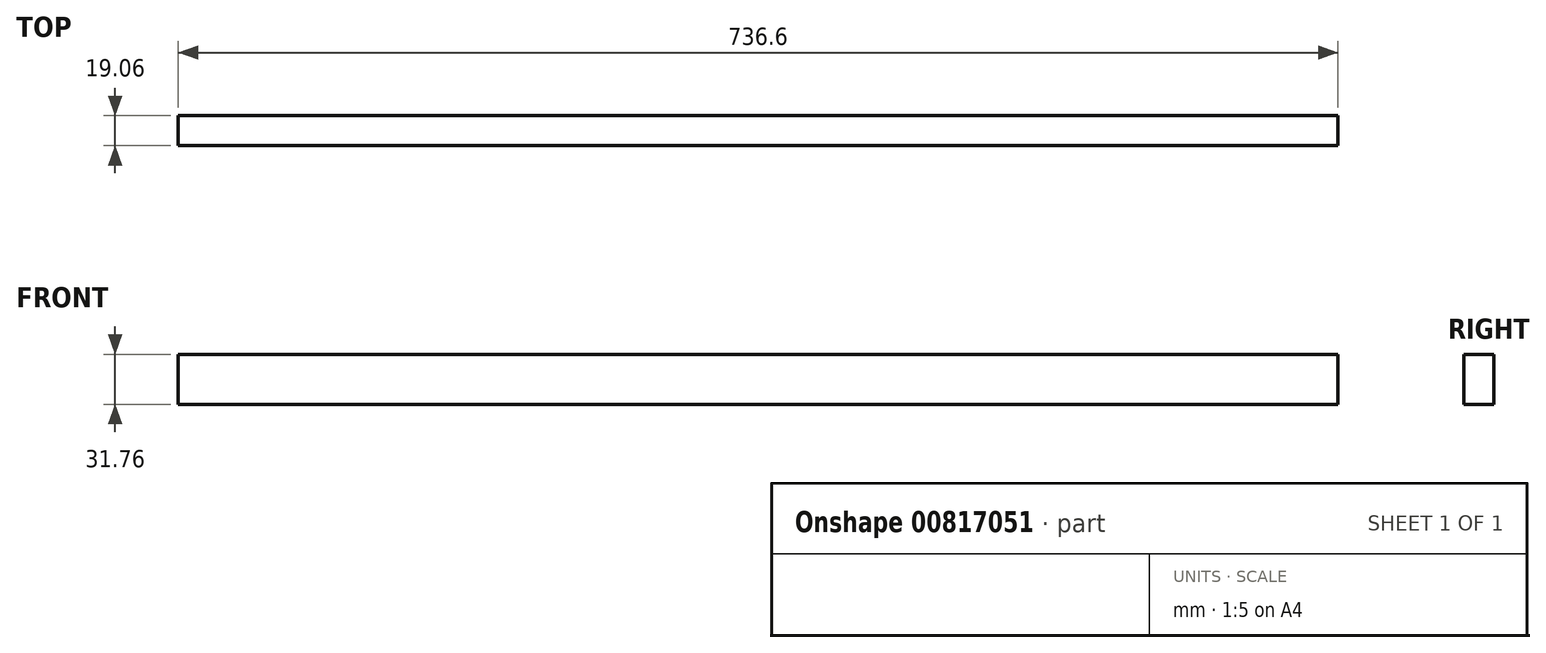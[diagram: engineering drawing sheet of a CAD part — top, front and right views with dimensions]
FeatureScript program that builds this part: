
annotation { "Feature Type Name" : "Feature", "Feature Type Description" : "" }
export const myFeature = defineFeature(function(context is Context, id is Id, definition is map)
    precondition{}
    {
        {
            var Q0;
            Q0=qCreatedBy(makeId("Right.planeOp"),FACE);
            var sketch = newSketch(context, id + "F0", { "sketchPlane" : qUnion([Q0])});
            skLineSegment(sketch, "E0.bottom", {"start": v(9.52, 15.88) * mm, "end": v(-9.52, 15.88) * mm});
            skLineSegment(sketch, "E0.top", {"start": v(9.52, -15.88) * mm, "end": v(-9.52, -15.88) * mm});
            skLineSegment(sketch, "E0.left", {"start": v(9.53, 15.88) * mm, "end": v(9.52, -15.88) * mm});
            skLineSegment(sketch, "E0.right", {"start": v(-9.52, 15.88) * mm, "end": v(-9.53, -15.88) * mm});
            skPoint(sketch, "E0.middle", {"position": v(0, 0) * mm});
            skSolve(sketch);
        }
        {
            var Q0;
            Q0=qSketchRegion(id+"F0",true);
            extrude(context, id + "F1", {"entities" : qUnion([Q0]), "depth" : 736.6 * mm, "offsetDistance" : 25.4 * mm});
        }
    });
